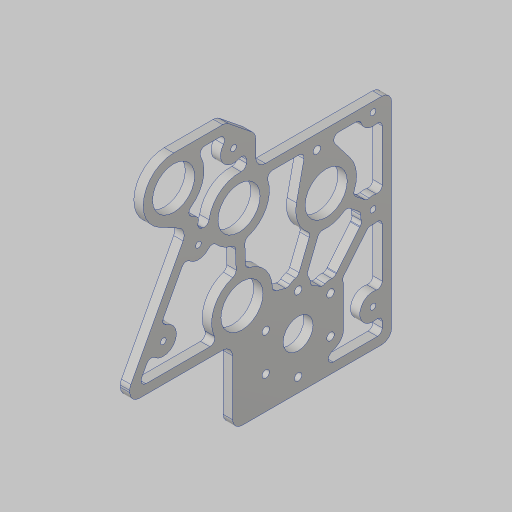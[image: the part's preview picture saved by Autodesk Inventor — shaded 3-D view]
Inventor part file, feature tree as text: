
AUTODESK INVENTOR PART (.ipt)
format: ipt  version: 2023.5 (Build 275446000, 446)  size: 630,272 bytes
history: native  units: in
note: dims shown in document units (in); Inventor stores cm internally (conversion verified against a paired STEP export)
features: sketch x7, extrude x5, hole x3, fillet x3, projected_geometry x3
ambient origin geometry x8: Origin, YZ Plane, XZ Plane, XY Plane, X Axis, Y Axis, Z Axis, Center Point
bodies: Solid1 (feature_tree)
feature tree (21):
  sketch  "Sketch1"  dims[d0=1.0in d1=12.0in]
  sketch  "Sketch2"  dims[d2=0.1924in d3=0.5in]
  extrude  "Extrusion1"  Depth=12.0in
  hole  "Hole1"  [1 undecoded]
  sketch  "Sketch3"  dims[d4=0.5in d5=0.5in]
  extrude  "Extrusion2"  Depth=0.5in
  hole  "Hole2"  [1 undecoded]
  extrude  "Extrusion3"  Depth=2.0in
  fillet  "Fillet1"  Radius=2.0in
  fillet  "Fillet2"  Radius=1.0in
  extrude  "Extrusion4"  Depth=2.0in
  hole  "Hole3"  [1 undecoded]
  extrude  "Extrusion5"  Depth=0.13in
  fillet  "Fillet3"  Radius=0.441in
  sketch  "Sketch4"  dims[d6=1.0in d7=11.067in]
  sketch  "Sketch5"  dims[d8=0.176in d9=1.176in d10=2.0in d11=1.0in]
  sketch  "Sketch6"  dims[d12=2.0in d13=1.0in]
  sketch  "Sketch7"  dims[d14=20.0in d15=3.572in d16=1.125in d17=0.441in d18=2.4in d19=1.375in d20=1.5in d21=0.5in d22=3.6in d23=1.0in d24=3.6in d25=1.0in d26=3.4in d27=3.342in d28=1.114in d29=5.9982in d30=1.5924in d31=7.8297in d32=1.5in d33=2.0in d34=1.125in d35=0.25in d37=0.5in d38=2.0in d39=4.0in d40=5.5in d41=1.0in d42=7.0in d43=7.5in d44=0.25in d45=0.0in d46=0.8in d47=0.5in d48=1.0in d49=4.0in d50=1.0in d51=4.5in d52=0.25in d53=0.25in d54=0.25in d55=2.0in d56=2.3622in d58=360.0deg d60=0.201in d61=0.75in d62=0.385in d63=0.25in d64=0.5635in d65=1.0in d66=0.8108in d67=0.25in d68=0.25in d69=0.0in d70=0.0in d71=0.156in d72=0.38in d73=0.375in d74=0.25in d75=0.5635in d76=1.0in d77=0.8108in d78=0.25in d79=0.25in d80=0.25in d81=0.125in d82=0.125in d83=0.125in d84=0.125in d85=0.125in d86=0.0in d87=0.0in d88=0.13in d89=0.26in d90=0.6in d91=1.125in d92=1.75in d93=1.5in d94=0.0in d95=0.0in d96=0.375in d97=2.0in d98=0.201in d99=0.75in d100=0.385in d101=0.25in d102=0.5635in d103=1.0in d104=0.8108in d105=0.25in d106=0.25in d107=0.25in d108=0.125in d109=0.125in d110=0.25in d111=0.125in d112=1.0in d113=0.0in d114=0.13in]
  projected_geometry  "Projected Loop1"
  projected_geometry  "Project Cut Edges1"
  projected_geometry  "Project Cut Edges2"
note: 3 required parameter values undecoded (feature->parameter linkage not recoverable at this tier; creation-order binding heuristic only, values carry confidence <= 0.55)
